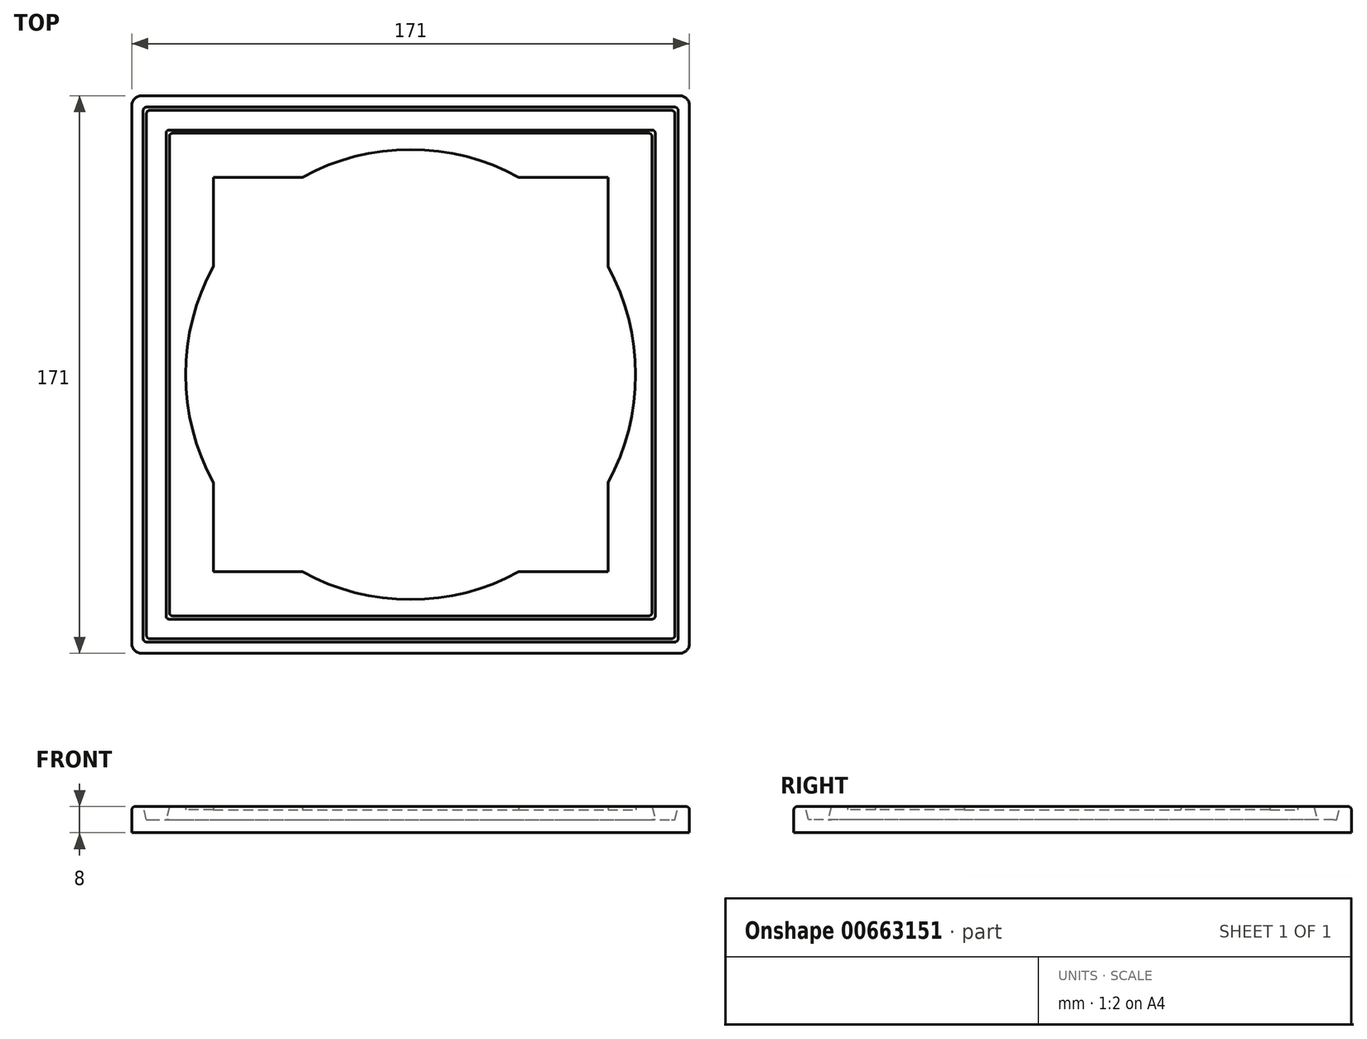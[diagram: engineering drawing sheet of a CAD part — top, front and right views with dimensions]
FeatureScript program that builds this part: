
annotation { "Feature Type Name" : "Feature", "Feature Type Description" : "" }
export const myFeature = defineFeature(function(context is Context, id is Id, definition is map)
    precondition{}
    {
        {
            var Q0;
            Q0=qCreatedBy(makeId("Top.planeOp"),FACE);
            var sketch = newSketch(context, id + "F0", { "sketchPlane" : qUnion([Q0])});
            skLineSegment(sketch, "E0.bottom", {"start": v(-85.5, 85.5) * mm, "end": v(85.5, 85.5) * mm});
            skLineSegment(sketch, "E0.top", {"start": v(-85.5, -85.5) * mm, "end": v(85.5, -85.5) * mm});
            skLineSegment(sketch, "E0.left", {"start": v(-85.5, 85.5) * mm, "end": v(-85.5, -85.5) * mm});
            skLineSegment(sketch, "E0.right", {"start": v(85.5, 85.5) * mm, "end": v(85.5, -85.5) * mm});
            skPoint(sketch, "E0.middle", {"position": v(0, 0) * mm});
            skLineSegment(sketch, "E1.bottom", {"start": v(-81, 81) * mm, "end": v(81, 81) * mm});
            skLineSegment(sketch, "E1.top", {"start": v(-81, -81) * mm, "end": v(81, -81) * mm});
            skLineSegment(sketch, "E1.left", {"start": v(-81, 81) * mm, "end": v(-81, -81) * mm});
            skLineSegment(sketch, "E1.right", {"start": v(81, 81) * mm, "end": v(81, -81) * mm});
            skLineSegment(sketch, "E2.bottom", {"start": v(-75, 75) * mm, "end": v(75, 75) * mm});
            skLineSegment(sketch, "E2.top", {"start": v(-75, -75) * mm, "end": v(75, -75) * mm});
            skLineSegment(sketch, "E2.left", {"start": v(-75, 75) * mm, "end": v(-75, -75) * mm});
            skLineSegment(sketch, "E2.right", {"start": v(75, 75) * mm, "end": v(75, -75) * mm});
            skLineSegment(sketch, "E3.bottom", {"start": v(-60.5, 60.5) * mm, "end": v(-33.18, 60.5) * mm});
            skLineSegment(sketch, "E3.top", {"start": v(-60.5, -60.5) * mm, "end": v(-33.18, -60.5) * mm});
            skLineSegment(sketch, "E3.left", {"start": v(-60.5, 60.5) * mm, "end": v(-60.5, 33.18) * mm});
            skLineSegment(sketch, "E3.right", {"start": v(60.5, 60.5) * mm, "end": v(60.5, 33.18) * mm});
            skArc(sketch, "E4", {"start": v(-60.5, 33.18) * mm, "mid": v(-69, 0) * mm, "end": v(-60.5, -33.18) * mm});
            skLineSegment(sketch, "E5.trimOffspring", {"start": v(33.18, 60.5) * mm, "end": v(60.5, 60.5) * mm});
            skArc(sketch, "E6.trimOffspring", {"start": v(33.18, 60.5) * mm, "mid": v(0, 69) * mm, "end": v(-33.18, 60.5) * mm});
            skLineSegment(sketch, "E7.trimOffspring", {"start": v(60.5, -33.18) * mm, "end": v(60.5, -60.5) * mm});
            skArc(sketch, "E8.trimOffspring", {"start": v(60.5, -33.18) * mm, "mid": v(69, 0) * mm, "end": v(60.5, 33.18) * mm});
            skLineSegment(sketch, "E9.trimOffspring", {"start": v(33.18, -60.5) * mm, "end": v(60.5, -60.5) * mm});
            skArc(sketch, "E10.trimOffspring", {"start": v(-33.18, -60.5) * mm, "mid": v(0, -69) * mm, "end": v(33.18, -60.5) * mm});
            skLineSegment(sketch, "E11.trimOffspring", {"start": v(-60.5, -33.18) * mm, "end": v(-60.5, -60.5) * mm});
            skSolve(sketch);
        }
        {
            var Q0;
            Q0 = qSketchRegion(id + "F0", true);
            extrude(context, id + "F1", {"entities" : qUnion([Q0]), "depth" : 8 * mm, "offsetDistance" : 25 * mm});
        }
        {
            var Q0;
            Q0=makeQuery(id+"F0.imprint","IMPRINT",FACE,{"disambiguationData":[TD([[makeQuery(id+"F0.imprint","IMPRINT",EDGE,{"derivedFrom":sQuery(id+"F0.wireOp",EDGE,"E1.bottom")}),-1.0]])]});
            extrude(context, id + "F2", {"entities" : qUnion([Q0]), "operationType" : NewBodyOperationType.ADD, "depth" : 4 * mm, "offsetDistance" : 25 * mm});
        }
        {
            var Q0;
            Q0=makeQuery(id+"F0.imprint","IMPRINT",FACE,{"disambiguationData":[TD([[makeQuery(id+"F0.imprint","IMPRINT",EDGE,{"derivedFrom":sQuery(id+"F0.wireOp",EDGE,"E2.bottom")}),-1.0]])]});
            extrude(context, id + "F3", {"entities" : qUnion([Q0]), "operationType" : NewBodyOperationType.ADD, "depth" : 8 * mm, "offsetDistance" : 25 * mm});
        }
        {
            var Q0;
            Q0=makeQuery(id+"F0.imprint","IMPRINT",FACE,{"disambiguationData":[TD([[makeQuery(id+"F0.imprint","IMPRINT",EDGE,{"derivedFrom":sQuery(id+"F0.wireOp",EDGE,"E3.bottom")}),-1.0]])]});
            extrude(context, id + "F4", {"entities" : qUnion([Q0]), "operationType" : NewBodyOperationType.ADD, "depth" : 7 * mm, "offsetDistance" : 25 * mm});
        }
        {
            var Q0;
            Q0=makeQuery(id+"F3.opExtrude","CAP_EDGE",EDGE,{"disambiguationData":[OSD([sQuery(id+"F0.wireOp",EDGE,"E2.left")])],"isStart":false});
            var Q1;
            Q1=makeQuery(id+"F3.opExtrude","CAP_EDGE",EDGE,{"disambiguationData":[OSD([sQuery(id+"F0.wireOp",EDGE,"E2.bottom")])],"isStart":false});
            var Q2;
            Q2=makeQuery(id+"F3.opExtrude","CAP_EDGE",EDGE,{"disambiguationData":[OSD([sQuery(id+"F0.wireOp",EDGE,"E2.top")])],"isStart":false});
            var Q3;
            Q3=makeQuery(id+"F3.opExtrude","CAP_EDGE",EDGE,{"disambiguationData":[OSD([sQuery(id+"F0.wireOp",EDGE,"E2.right")])],"isStart":false});
            chamfer(context, id + "F5", {"entities" : qUnion([Q0, Q1, Q2, Q3]), "chamferType" : ChamferType.TWO_OFFSETS, "width1" : 1 * mm, "oppositeDirection" : false, "width2" : 4 * mm, "tangentPropagation" : true});
        }
        {
            var Q0;
            Q0=makeQuery(id+"F1.opExtrude","CAP_EDGE",EDGE,{"disambiguationData":[OSD([sQuery(id+"F0.wireOp",EDGE,"E1.bottom")])],"isStart":false});
            var Q1;
            Q1=makeQuery(id+"F1.opExtrude","CAP_EDGE",EDGE,{"disambiguationData":[OSD([sQuery(id+"F0.wireOp",EDGE,"E1.right")])],"isStart":false});
            var Q2;
            Q2=makeQuery(id+"F1.opExtrude","CAP_EDGE",EDGE,{"disambiguationData":[OSD([sQuery(id+"F0.wireOp",EDGE,"E1.top")])],"isStart":false});
            var Q3;
            Q3=makeQuery(id+"F1.opExtrude","CAP_EDGE",EDGE,{"disambiguationData":[OSD([sQuery(id+"F0.wireOp",EDGE,"E1.left")])],"isStart":false});
            chamfer(context, id + "F6", {"entities" : qUnion([Q0, Q1, Q2, Q3]), "chamferType" : ChamferType.TWO_OFFSETS, "width1" : 1 * mm, "oppositeDirection" : false, "width2" : 4 * mm, "tangentPropagation" : true});
        }
        {
            var Q0;
            Q0=makeQuery(id+"F1.opExtrude","CAP_EDGE",EDGE,{"disambiguationData":[OSD([sQuery(id+"F0.wireOp",EDGE,"E0.right")])],"isStart":false});
            var Q1;
            Q1=makeQuery(id+"F1.opExtrude","CAP_EDGE",EDGE,{"disambiguationData":[OSD([sQuery(id+"F0.wireOp",EDGE,"E0.top")])],"isStart":false});
            var Q2;
            Q2=makeQuery(id+"F1.opExtrude","CAP_EDGE",EDGE,{"disambiguationData":[OSD([sQuery(id+"F0.wireOp",EDGE,"E0.left")])],"isStart":false});
            var Q3;
            Q3=makeQuery(id+"F1.opExtrude","CAP_EDGE",EDGE,{"disambiguationData":[OSD([sQuery(id+"F0.wireOp",EDGE,"E0.bottom")])],"isStart":false});
            fillet(context, id + "F7", {"entities" : qUnion([Q0, Q1, Q2, Q3]), "radius" : 1 * mm, "tangentPropagation" : true, "allowEdgeOverflow" : false});
        }
        {
            var Q0;
            Q0=makeQuery(id+"F5.opChamfer","BLEND_EDGE",EDGE,{"blendedFrom":[makeQuery(id+"F3.opExtrude","CAP_EDGE",EDGE,{"disambiguationData":[OSD([sQuery(id+"F0.wireOp",EDGE,"E2.top")])],"isStart":false}),makeQuery(id+"F3.opExtrude","CAP_EDGE",EDGE,{"disambiguationData":[OSD([sQuery(id+"F0.wireOp",EDGE,"E2.right")])],"isStart":false})],"blendedInto":[]});
            var Q1;
            Q1=makeQuery(id+"F5.opChamfer","BLEND_EDGE",EDGE,{"blendedFrom":[makeQuery(id+"F3.opExtrude","CAP_EDGE",EDGE,{"disambiguationData":[OSD([sQuery(id+"F0.wireOp",EDGE,"E2.top")])],"isStart":false}),makeQuery(id+"F3.opExtrude","CAP_EDGE",EDGE,{"disambiguationData":[OSD([sQuery(id+"F0.wireOp",EDGE,"E2.left")])],"isStart":false})],"blendedInto":[]});
            var Q2;
            Q2=makeQuery(id+"F5.opChamfer","BLEND_EDGE",EDGE,{"blendedFrom":[makeQuery(id+"F3.opExtrude","CAP_EDGE",EDGE,{"disambiguationData":[OSD([sQuery(id+"F0.wireOp",EDGE,"E2.bottom")])],"isStart":false}),makeQuery(id+"F3.opExtrude","CAP_EDGE",EDGE,{"disambiguationData":[OSD([sQuery(id+"F0.wireOp",EDGE,"E2.left")])],"isStart":false})],"blendedInto":[]});
            var Q3;
            Q3=makeQuery(id+"F5.opChamfer","BLEND_EDGE",EDGE,{"blendedFrom":[makeQuery(id+"F3.opExtrude","CAP_EDGE",EDGE,{"disambiguationData":[OSD([sQuery(id+"F0.wireOp",EDGE,"E2.bottom")])],"isStart":false}),makeQuery(id+"F3.opExtrude","CAP_EDGE",EDGE,{"disambiguationData":[OSD([sQuery(id+"F0.wireOp",EDGE,"E2.right")])],"isStart":false})],"blendedInto":[]});
            var Q4;
            Q4=makeQuery(id+"F6.opChamfer","BLEND_EDGE",EDGE,{"blendedFrom":[makeQuery(id+"F1.opExtrude","CAP_EDGE",EDGE,{"disambiguationData":[OSD([sQuery(id+"F0.wireOp",EDGE,"E1.bottom")])],"isStart":false}),makeQuery(id+"F1.opExtrude","CAP_EDGE",EDGE,{"disambiguationData":[OSD([sQuery(id+"F0.wireOp",EDGE,"E1.left")])],"isStart":false})],"blendedInto":[]});
            var Q5;
            Q5=makeQuery(id+"F6.opChamfer","BLEND_EDGE",EDGE,{"blendedFrom":[makeQuery(id+"F1.opExtrude","CAP_EDGE",EDGE,{"disambiguationData":[OSD([sQuery(id+"F0.wireOp",EDGE,"E1.bottom")])],"isStart":false}),makeQuery(id+"F1.opExtrude","CAP_EDGE",EDGE,{"disambiguationData":[OSD([sQuery(id+"F0.wireOp",EDGE,"E1.right")])],"isStart":false})],"blendedInto":[]});
            var Q6;
            Q6=makeQuery(id+"F6.opChamfer","BLEND_EDGE",EDGE,{"blendedFrom":[makeQuery(id+"F1.opExtrude","CAP_EDGE",EDGE,{"disambiguationData":[OSD([sQuery(id+"F0.wireOp",EDGE,"E1.top")])],"isStart":false}),makeQuery(id+"F1.opExtrude","CAP_EDGE",EDGE,{"disambiguationData":[OSD([sQuery(id+"F0.wireOp",EDGE,"E1.right")])],"isStart":false})],"blendedInto":[]});
            var Q7;
            Q7=makeQuery(id+"F6.opChamfer","BLEND_EDGE",EDGE,{"blendedFrom":[makeQuery(id+"F1.opExtrude","CAP_EDGE",EDGE,{"disambiguationData":[OSD([sQuery(id+"F0.wireOp",EDGE,"E1.top")])],"isStart":false}),makeQuery(id+"F1.opExtrude","CAP_EDGE",EDGE,{"disambiguationData":[OSD([sQuery(id+"F0.wireOp",EDGE,"E1.left")])],"isStart":false})],"blendedInto":[]});
            fillet(context, id + "F8", {"entities" : qUnion([Q0, Q1, Q2, Q3, Q4, Q5, Q6, Q7]), "radius" : 1 * mm, "tangentPropagation" : true, "allowEdgeOverflow" : false});
        }
        {
            var Q0;
            Q0=makeQuery(id+"F1.opExtrude","SWEPT_EDGE",EDGE,{"disambiguationData":[OSD([sQuery(id+"F0.wireOp",EDGE,"E0.top"),sQuery(id+"F0.wireOp",EDGE,"E0.left")])]});
            var Q1;
            Q1=makeQuery(id+"F1.opExtrude","SWEPT_EDGE",EDGE,{"disambiguationData":[OSD([sQuery(id+"F0.wireOp",EDGE,"E0.top"),sQuery(id+"F0.wireOp",EDGE,"E0.right")])]});
            var Q2;
            Q2=makeQuery(id+"F1.opExtrude","SWEPT_EDGE",EDGE,{"disambiguationData":[OSD([sQuery(id+"F0.wireOp",EDGE,"E0.bottom"),sQuery(id+"F0.wireOp",EDGE,"E0.left")])]});
            var Q3;
            Q3=makeQuery(id+"F1.opExtrude","SWEPT_EDGE",EDGE,{"disambiguationData":[OSD([sQuery(id+"F0.wireOp",EDGE,"E0.bottom"),sQuery(id+"F0.wireOp",EDGE,"E0.right")])]});
            fillet(context, id + "F9", {"entities" : qUnion([Q0, Q1, Q2, Q3]), "radius" : 3 * mm, "tangentPropagation" : true, "allowEdgeOverflow" : false});
        }
    });
